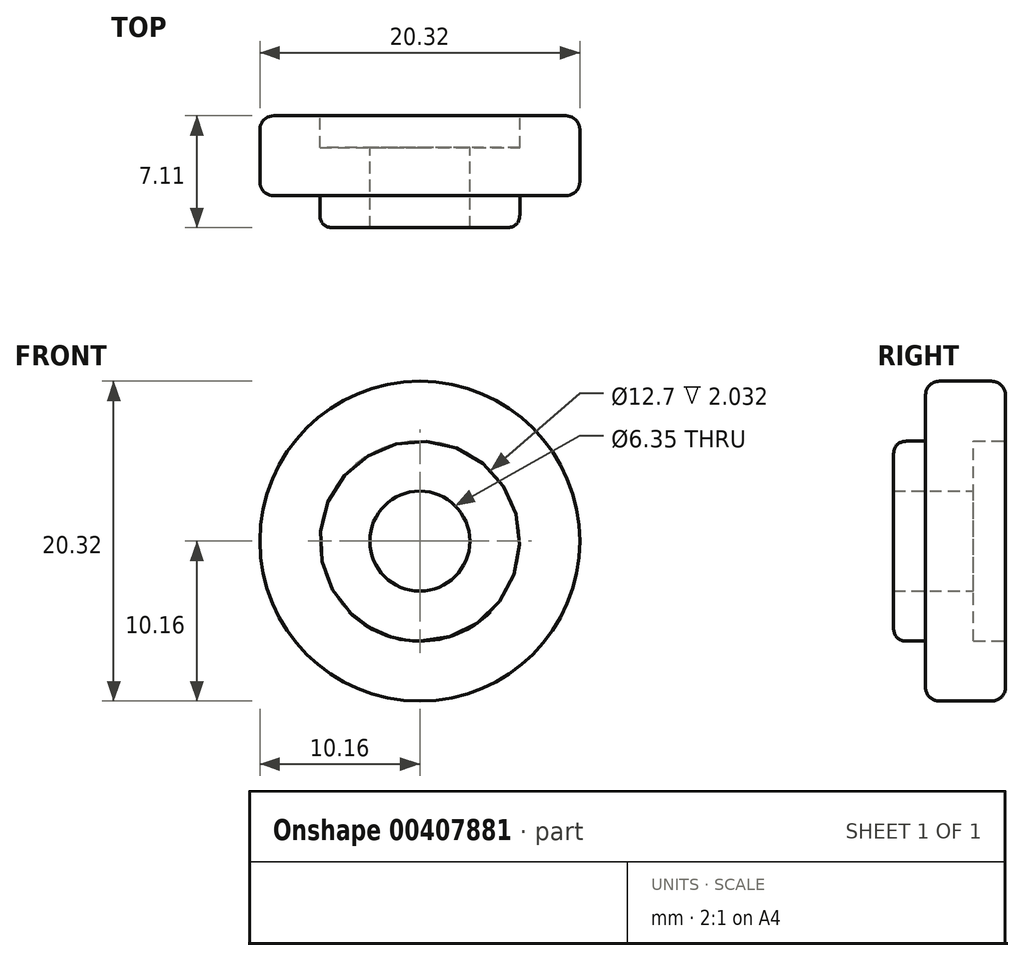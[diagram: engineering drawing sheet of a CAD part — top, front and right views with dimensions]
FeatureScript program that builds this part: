
annotation { "Feature Type Name" : "Feature", "Feature Type Description" : "" }
export const myFeature = defineFeature(function(context is Context, id is Id, definition is map)
    precondition{}
    {
        {
            var Q0;
            Q0=qCreatedBy(makeId("Front.planeOp"),FACE);
            var sketch = newSketch(context, id + "F0", { "sketchPlane" : qUnion([Q0])});
            skCircle(sketch, "E0", {"center": v(0, 0) * mm, "radius": 10.16 * mm});
            skSolve(sketch);
        }
        {
            var Q0;
            Q0 = qSketchRegion(id + "F0", true);
            extrude(context, id + "F1", {"entities" : qUnion([Q0]), "depth" : 5.08 * mm});
        }
        {
            var Q0;
            Q0=qCreatedBy(makeId("Front.planeOp"),FACE);
            var sketch = newSketch(context, id + "F2", { "sketchPlane" : qUnion([Q0])});
            skCircle(sketch, "E1", {"center": v(0, 0) * mm, "radius": 6.35 * mm});
            skSolve(sketch);
        }
        {
            var Q0;
            Q0 = qSketchRegion(id + "F2", true);
            extrude(context, id + "F3", {"entities" : qUnion([Q0]), "operationType" : NewBodyOperationType.ADD, "depth" : 7.11 * mm});
        }
        {
            var Q0;
            Q0=qCreatedBy(makeId("Front.planeOp"),FACE);
            var sketch = newSketch(context, id + "F4", { "sketchPlane" : qUnion([Q0])});
            skCircle(sketch, "E2", {"center": v(0, 0) * mm, "radius": 6.35 * mm});
            skSolve(sketch);
        }
        {
            var Q0;
            Q0 = qSketchRegion(id + "F4", true);
            extrude(context, id + "F5", {"entities" : qUnion([Q0]), "operationType" : NewBodyOperationType.REMOVE, "depth" : 2.03 * mm, "hasSecondDirection" : true, "secondDirectionOppositeDirection" : true, "secondDirectionDepth" : 7.11 * mm});
        }
        {
            var Q0;
            Q0=qCreatedBy(makeId("Front.planeOp"),FACE);
            var sketch = newSketch(context, id + "F6", { "sketchPlane" : qUnion([Q0])});
            skCircle(sketch, "E3", {"center": v(0, 0) * mm, "radius": 3.18 * mm});
            skSolve(sketch);
        }
        {
            var Q0;
            Q0 = qSketchRegion(id + "F6", true);
            extrude(context, id + "F7", {"entities" : qUnion([Q0]), "operationType" : NewBodyOperationType.REMOVE, "endBound" : BoundingType.THROUGH_ALL, "depth" : 7.11 * mm});
        }
        {
            var Q0;
            Q0=makeQuery(id+"F1.opExtrude","CAP_EDGE",EDGE,{"disambiguationData":[OSD([sQuery(id+"F0.wireOp",EDGE,"E0")])],"isStart":true});
            fillet(context, id + "F8", {"entities" : qUnion([Q0]), "radius" : 0.89 * mm, "tangentPropagation" : true, "allowEdgeOverflow" : false});
        }
        {
            var Q0;
            Q0=makeQuery(id+"F1.opExtrude","CAP_EDGE",EDGE,{"disambiguationData":[OSD([sQuery(id+"F0.wireOp",EDGE,"E0")])],"isStart":false});
            fillet(context, id + "F9", {"entities" : qUnion([Q0]), "radius" : 0.89 * mm, "tangentPropagation" : true, "allowEdgeOverflow" : false});
        }
        {
            var Q0;
            Q0=makeQuery(id+"F3.opExtrude","CAP_EDGE",EDGE,{"disambiguationData":[OSD([sQuery(id+"F2.wireOp",EDGE,"E1")])],"isStart":false});
            fillet(context, id + "F10", {"entities" : qUnion([Q0]), "radius" : 0.89 * mm, "rho" : 0.5, "crossSection" : FilletCrossSection.CONIC, "allowEdgeOverflow" : false});
        }
    });
